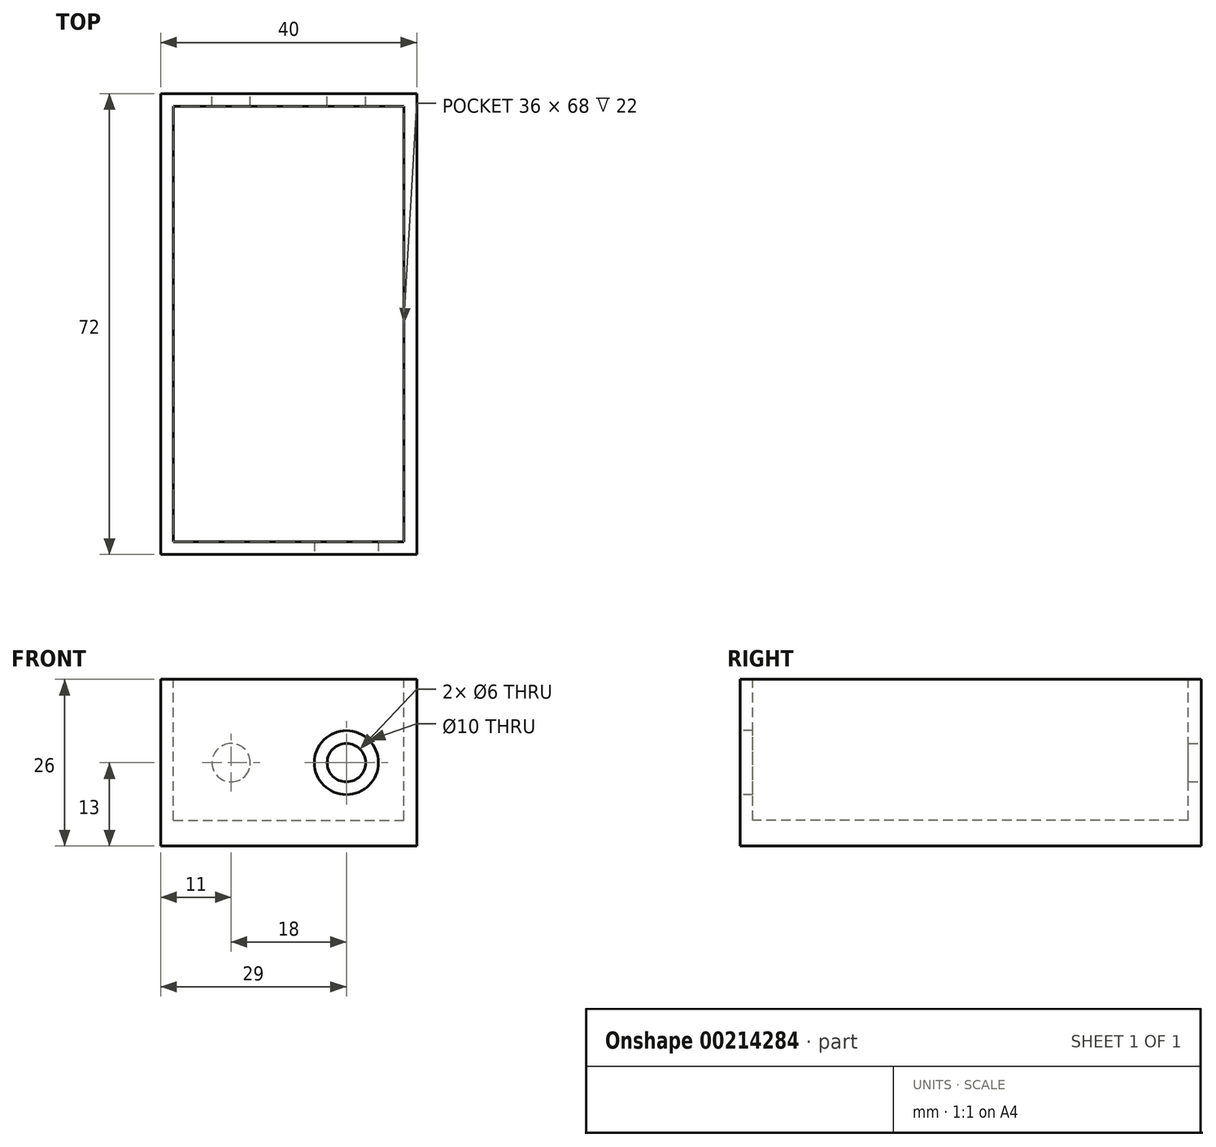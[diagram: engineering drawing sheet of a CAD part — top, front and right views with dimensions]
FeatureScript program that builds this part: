
annotation { "Feature Type Name" : "Feature", "Feature Type Description" : "" }
export const myFeature = defineFeature(function(context is Context, id is Id, definition is map)
    precondition{}
    {
        {
            var Q0;
            Q0=qCreatedBy(makeId("Top.planeOp"),FACE);
            var sketch = newSketch(context, id + "F0", { "sketchPlane" : qUnion([Q0])});
            skLineSegment(sketch, "E0.bottom", {"start": v(-20, 36) * mm, "end": v(20, 36) * mm});
            skLineSegment(sketch, "E0.top", {"start": v(-20, -36) * mm, "end": v(20, -36) * mm});
            skLineSegment(sketch, "E0.left", {"start": v(-20, 36) * mm, "end": v(-20, -36) * mm});
            skLineSegment(sketch, "E0.right", {"start": v(20, 36) * mm, "end": v(20, -36) * mm});
            skPoint(sketch, "E0.middle", {"position": v(0, 0) * mm});
            skSolve(sketch);
        }
        {
            var Q0;
            Q0 = qSketchRegion(id + "F0", true);
            extrude(context, id + "F1", {"entities" : qUnion([Q0]), "depth" : 26 * mm});
        }
        {
            var Q0;
            Q0=makeQuery(id+"F1.opExtrude","CAP_FACE",FACE,{"disambiguationData":[OSD([sQuery(id+"F0.wireOp",EDGE,"E0.bottom"),sQuery(id+"F0.wireOp",EDGE,"E0.top"),sQuery(id+"F0.wireOp",EDGE,"E0.left"),sQuery(id+"F0.wireOp",EDGE,"E0.right")])],"isStart":false});
            var sketch = newSketch(context, id + "F2", { "sketchPlane" : qUnion([Q0])});
            skLineSegment(sketch, "E1.bottom", {"start": v(-18, 34) * mm, "end": v(18, 34) * mm});
            skLineSegment(sketch, "E1.top", {"start": v(-18, -34) * mm, "end": v(18, -34) * mm});
            skLineSegment(sketch, "E1.left", {"start": v(-18, 34) * mm, "end": v(-18, -34) * mm});
            skLineSegment(sketch, "E1.right", {"start": v(18, 34) * mm, "end": v(18, -34) * mm});
            skPoint(sketch, "E1.middle", {"position": v(0, 0) * mm});
            skSolve(sketch);
        }
        {
            var Q0;
            Q0 = qSketchRegion(id + "F2", true);
            extrude(context, id + "F3", {"entities" : qUnion([Q0]), "operationType" : NewBodyOperationType.REMOVE, "oppositeDirection" : true, "depth" : (26 - 4) * mm});
        }
        {
            var Q0;
            Q0=makeQuery(id+"F1.opExtrude","SWEPT_FACE",FACE,{"disambiguationData":[OSD([sQuery(id+"F0.wireOp",EDGE,"E0.top")])]});
            var sketch = newSketch(context, id + "F4", { "sketchPlane" : qUnion([Q0])});
            skCircle(sketch, "E2", {"center": v(9, 13) * mm, "radius": 5 * mm});
            skSolve(sketch);
        }
        {
            var Q0;
            Q0 = qSketchRegion(id + "F4", true);
            extrude(context, id + "F5", {"entities" : qUnion([Q0]), "operationType" : NewBodyOperationType.REMOVE, "oppositeDirection" : true, "depth" : 25 * mm});
        }
        {
            var Q0;
            Q0=makeQuery(id+"F1.opExtrude","SWEPT_FACE",FACE,{"disambiguationData":[OSD([sQuery(id+"F0.wireOp",EDGE,"E0.bottom")])]});
            var sketch = newSketch(context, id + "F6", { "sketchPlane" : qUnion([Q0])});
            skCircle(sketch, "E3", {"center": v(-9, 13) * mm, "radius": 3 * mm});
            skCircle(sketch, "E4", {"center": v(9, 13) * mm, "radius": 3 * mm});
            skSolve(sketch);
        }
        {
            var Q0;
            Q0 = qSketchRegion(id + "F6", true);
            extrude(context, id + "F7", {"entities" : qUnion([Q0]), "operationType" : NewBodyOperationType.REMOVE, "oppositeDirection" : true, "depth" : 25 * mm});
        }
    });
